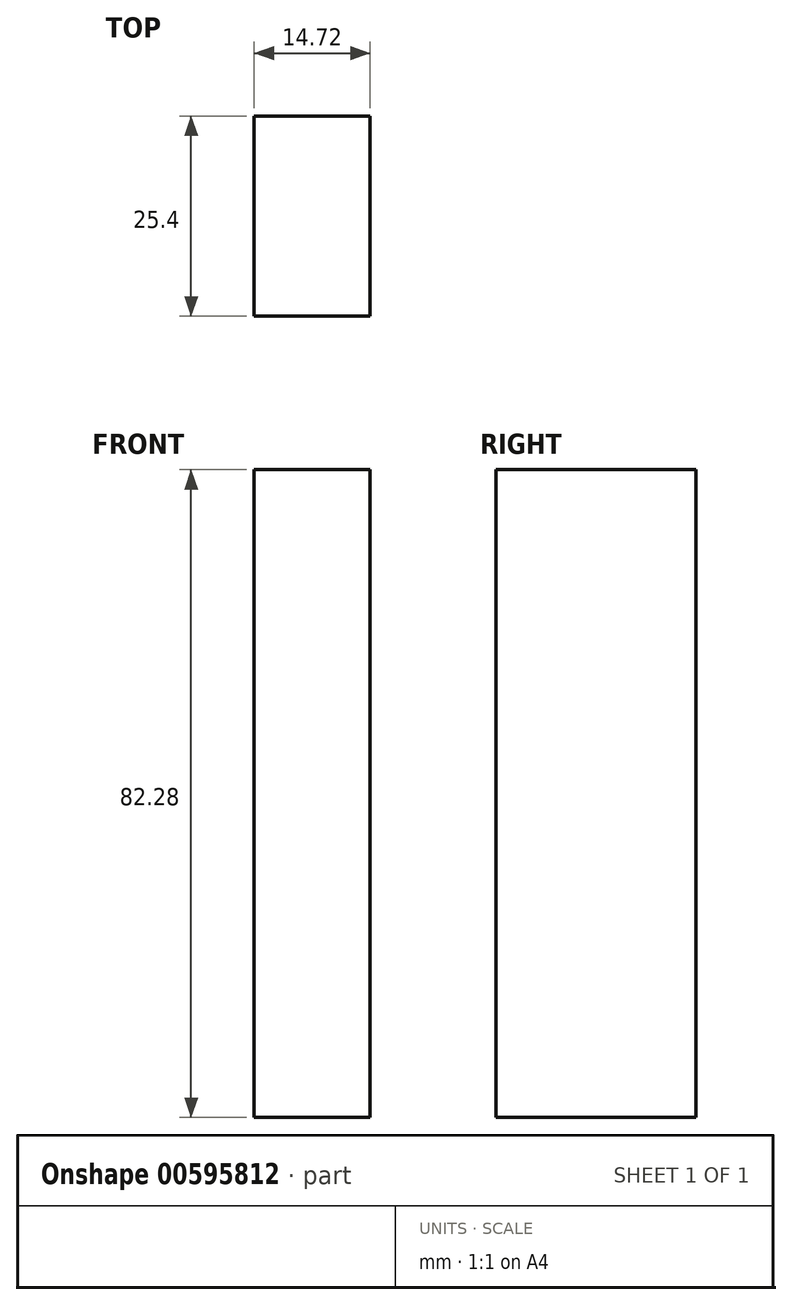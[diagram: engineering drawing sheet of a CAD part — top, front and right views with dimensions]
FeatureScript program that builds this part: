
annotation { "Feature Type Name" : "Feature", "Feature Type Description" : "" }
export const myFeature = defineFeature(function(context is Context, id is Id, definition is map)
    precondition{}
    {
        {
            var Q0;
            Q0=qCreatedBy(makeId("Front.planeOp"),FACE);
            var sketch = newSketch(context, id + "F0", { "sketchPlane" : qUnion([Q0])});
            skLineSegment(sketch, "E0.bottom", {"start": v(0, 33.78) * mm, "end": v(14.72, 33.78) * mm});
            skLineSegment(sketch, "E0.top", {"start": v(0, -48.5) * mm, "end": v(14.72, -48.5) * mm});
            skLineSegment(sketch, "E0.left", {"start": v(0, 33.78) * mm, "end": v(0, -48.5) * mm});
            skLineSegment(sketch, "E0.right", {"start": v(14.72, 33.78) * mm, "end": v(14.72, -48.5) * mm});
            skSolve(sketch);
        }
        {
            var Q0;
            Q0 = qSketchRegion(id + "F0", true);
            extrude(context, id + "F1", {"entities" : qUnion([Q0]), "depth" : 25.4 * mm, "offsetDistance" : 25.4 * mm});
        }
    });
